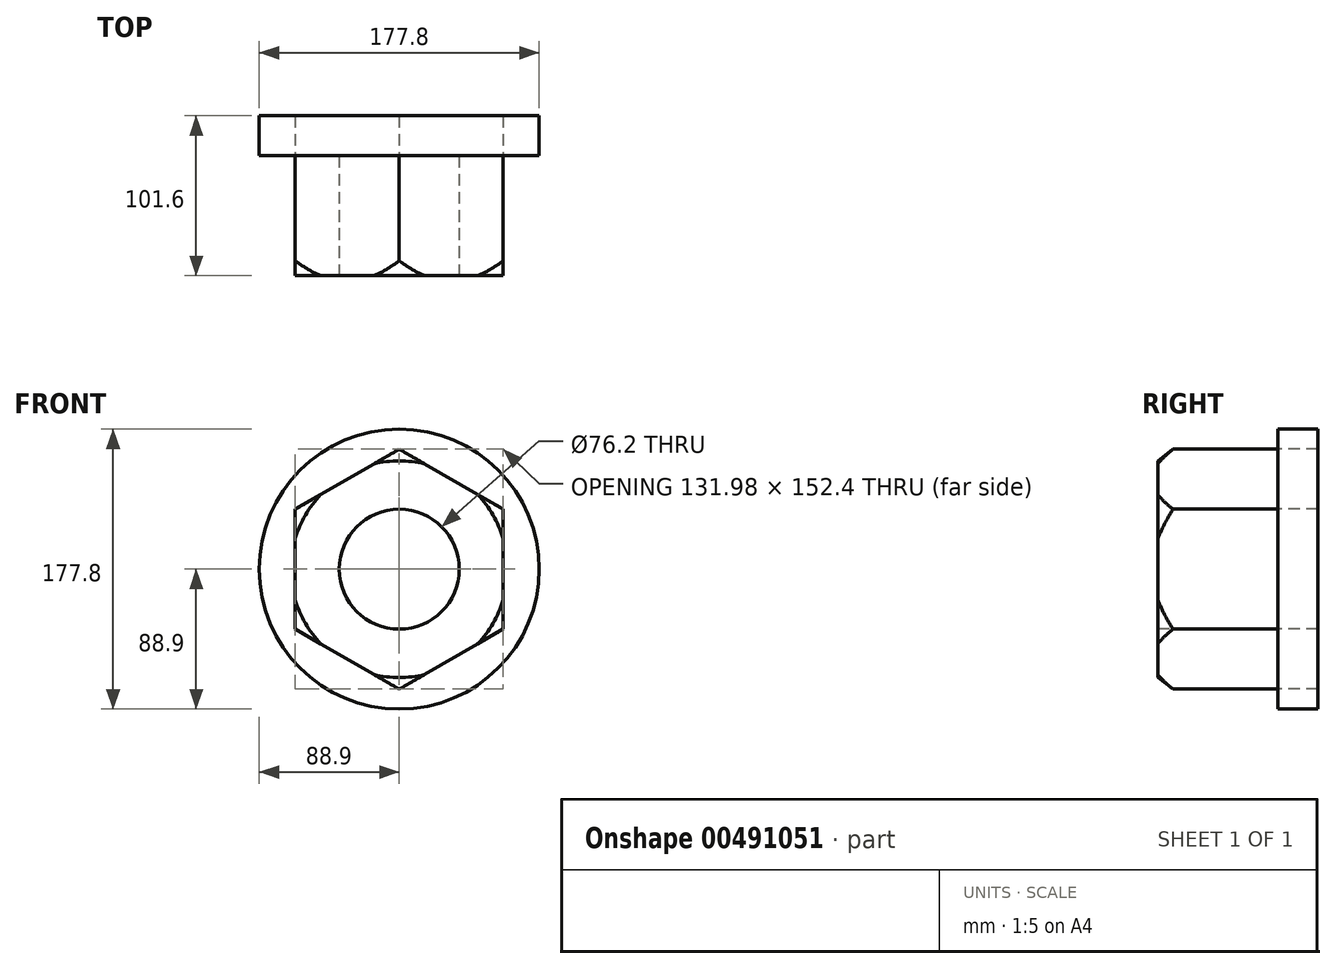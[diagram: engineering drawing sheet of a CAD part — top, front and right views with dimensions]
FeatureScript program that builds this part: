
annotation { "Feature Type Name" : "Feature", "Feature Type Description" : "" }
export const myFeature = defineFeature(function(context is Context, id is Id, definition is map)
    precondition{}
    {
        {
            var Q0;
            Q0=qCreatedBy(makeId("Front.planeOp"),FACE);
            var sketch = newSketch(context, id + "F0", { "sketchPlane" : qUnion([Q0])});
            skLineSegment(sketch, "E0", {"start": v(0, 0) * mm, "end": v(0, 76.2) * mm});
            skLineSegment(sketch, "E1", {"start": v(0, 76.2) * mm, "end": v(-66, 38.1) * mm});
            skLineSegment(sketch, "E2", {"start": v(-66, 38.1) * mm, "end": v(-66, -38.1) * mm});
            skLineSegment(sketch, "E3.MirrorCS", {"start": v(0, -76.2) * mm, "end": v(-66, -38.1) * mm});
            skLineSegment(sketch, "E4.MirrorCS", {"start": v(0, 76.2) * mm, "end": v(66, 38.1) * mm});
            skLineSegment(sketch, "E5.MirrorCS", {"start": v(66, 38.1) * mm, "end": v(66, -38.1) * mm});
            skLineSegment(sketch, "E6.MirrorCS", {"start": v(0, -76.2) * mm, "end": v(66, -38.1) * mm});
            skSolve(sketch);
        }
        {
            var Q0;
            Q0=makeQuery(id+"F0.imprint","IMPRINT",FACE,{"disambiguationData":[TD([[makeQuery(id+"F0.imprint","IMPRINT",EDGE,{"derivedFrom":sQuery(id+"F0.wireOp",EDGE,"E1")}),1.0]])]});
            extrude(context, id + "F1", {"entities" : qUnion([Q0]), "depth" : 76.2 * mm});
        }
        {
            var Q0;
            Q0=makeQuery(id+"F1.opExtrude","CAP_FACE",FACE,{"disambiguationData":[OSD([sQuery(id+"F0.wireOp",EDGE,"E1"),sQuery(id+"F0.wireOp",EDGE,"E2"),sQuery(id+"F0.wireOp",EDGE,"E3.MirrorCS"),sQuery(id+"F0.wireOp",EDGE,"E4.MirrorCS"),sQuery(id+"F0.wireOp",EDGE,"E5.MirrorCS"),sQuery(id+"F0.wireOp",EDGE,"E6.MirrorCS")])],"isStart":true});
            var sketch = newSketch(context, id + "F2", { "sketchPlane" : qUnion([Q0])});
            skCircle(sketch, "E7", {"center": v(0, 0) * mm, "radius": 88.9 * mm});
            skSolve(sketch);
        }
        {
            var Q0;
            Q0=makeQuery(id+"F2.imprint","IMPRINT",FACE,{"disambiguationData":[TD([[makeQuery(id+"F2.imprint","IMPRINT",EDGE,{"derivedFrom":sQuery(id+"F2.wireOp",EDGE,"E7")}),1.0]])]});
            extrude(context, id + "F3", {"entities" : qUnion([Q0]), "depth" : 25.4 * mm});
        }
        {
            var Q0;
            Q0=makeQuery(id+"F1.opExtrude","CAP_FACE",FACE,{"disambiguationData":[OSD([sQuery(id+"F0.wireOp",EDGE,"E1"),sQuery(id+"F0.wireOp",EDGE,"E2"),sQuery(id+"F0.wireOp",EDGE,"E3.MirrorCS"),sQuery(id+"F0.wireOp",EDGE,"E4.MirrorCS"),sQuery(id+"F0.wireOp",EDGE,"E5.MirrorCS"),sQuery(id+"F0.wireOp",EDGE,"E6.MirrorCS")])],"isStart":false});
            var sketch = newSketch(context, id + "F4", { "sketchPlane" : qUnion([Q0])});
            skCircle(sketch, "E8", {"center": v(0, 0) * mm, "radius": 38.1 * mm});
            skSolve(sketch);
        }
        {
            var Q0;
            Q0=makeQuery(id+"F4.imprint","IMPRINT",FACE,{"disambiguationData":[TD([[makeQuery(id+"F4.imprint","IMPRINT",EDGE,{"derivedFrom":sQuery(id+"F4.wireOp",EDGE,"E8")}),1.0]])]});
            extrude(context, id + "F5", {"entities" : qUnion([Q0]), "operationType" : NewBodyOperationType.REMOVE, "endBound" : BoundingType.THROUGH_ALL, "oppositeDirection" : true, "depth" : 25.4 * mm});
        }
        {
            var Q0;
            Q0=qCreatedBy(makeId("Right.planeOp"),FACE);
            var sketch = newSketch(context, id + "F6", { "sketchPlane" : qUnion([Q0])});
            skLineSegment(sketch, "E9", {"start": v(-79.41, 66.31) * mm, "end": v(-61.86, 79.97) * mm});
            skLineSegment(sketch, "E10", {"start": v(-61.86, 79.97) * mm, "end": v(-79.55, 79.97) * mm});
            skLineSegment(sketch, "E11", {"start": v(-79.55, 79.97) * mm, "end": v(-79.41, 66.31) * mm});
            skSolve(sketch);
        }
        {
            var Q0;
            Q0=makeQuery(id+"F6.imprint","IMPRINT",FACE,{"disambiguationData":[TD([[makeQuery(id+"F6.imprint","IMPRINT",EDGE,{"derivedFrom":sQuery(id+"F6.wireOp",EDGE,"E9")}),1.0]])]});
            var Q1;
            Q1=makeQuery(id+"F5.boolean.opBoolean","COPY",FACE,{"derivedFrom":makeQuery(id+"F5.opExtrude","SWEPT_FACE",FACE,{"disambiguationData":[OSD([sQuery(id+"F4.wireOp",EDGE,"E8")])]})});
            revolve(context, id + "F7", {"operationType" : NewBodyOperationType.REMOVE, "entities" : qUnion([Q0]), "axis" : qUnion([Q1]), "revolveType" : RevolveType.FULL, "oppositeDirection" : true});
        }
    });
